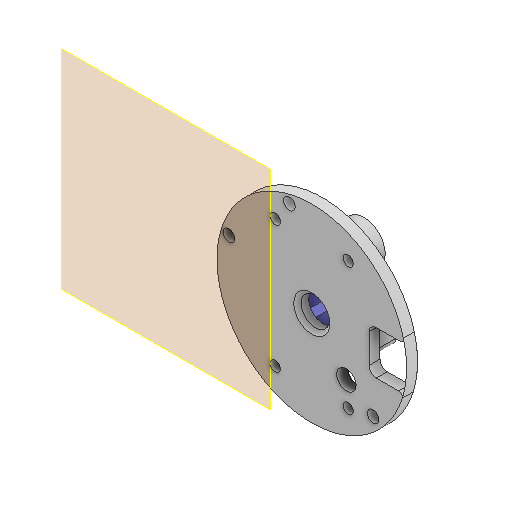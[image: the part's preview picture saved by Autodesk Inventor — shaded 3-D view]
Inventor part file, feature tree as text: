
AUTODESK INVENTOR PART (.ipt)
format: ipt  version: 2022 (Build 260153000, 153)  size: 510,976 bytes
history: native  units: in
note: dims shown in document units (in); Inventor stores cm internally (conversion verified against a paired STEP export)
features: reference x12, extrude x8, sketch x7, other x5, plane x4, fillet x1, chamfer x1, projected_geometry x1
ambient origin geometry x8: Origin, YZ Plane, XZ Plane, XY Plane, X Axis, Y Axis, Z Axis, Center Point
bodies: Solid1 (feature_tree)
feature tree (39):
  plane  "Work Plane1"
  extrude  "Extrusion1"  Depth=0.1181in
  extrude  "Extrusion2"  Depth=1.0in
  plane  "Arbeitsebene4"
  extrude  "Extrusion5"  TaperAngle=0.0deg  [1 undecoded]
  plane  "Arbeitsebene3"
  extrude  "Extrusion6"  Depth=0.126in
  plane  "Arbeitsebene2"
  extrude  "Extrusion7"  Depth=0.0787in
  extrude  "Extrusion10"  Depth=0.0394in TaperAngle=0.0deg
  extrude  "Extrusion11"  Depth=0.3937in
  fillet  "Rundung1"  Radius=0.3543in
  chamfer  "Fase4"  Distance=0.7165in
  extrude  "Extrusion14"  Depth=0.1181in
  sketch  "Sketch1"  dims[d0=0.1181in d1=0.0in d2=0.315in]
  reference  "Reference1"
  reference  "Reference2"
  reference  "Reference3"
  reference  "Reference4"
  reference  "Reference5"
  reference  "Reference6"
  reference  "Reference7"
  reference  "Reference8"
  sketch  "Sketch2"  dims[d3=0.311in d4=1.0in d5=-0.0137in]
  sketch  "Sketch7"  dims[d30=0.1102in d31=0.0in d32=0.0in]
  sketch  "Sketch8"  dims[d33=0.126in d34=0.126in]
  sketch  "Sketch9"  dims[d35=0.0in d36=0.0in d37=0.0787in]
  sketch  "Skizze12"  dims[d38=0.0004in d39=0.0in d51=0.0394in d52=0.0in]
  projected_geometry  "Projizierte Kontur2"
  sketch  "Skizze16"  dims[d53=0.2638in d54=0.3937in d55=0.3543in d56=0.0in d65=0.7165in d66=0.7165in d67=0.0787in d68=0.0787in d71=0.315in d72=0.315in d73=0.315in d74=0.315in d75=0.0394in d76=0.0787in d77=45.0deg d78=0.126in d79=0.1181in d80=0.0in d81=0.0197in d82=0.0344in]
  reference  "Referenz30"
  reference  "Referenz31"
  reference  "Referenz32"
  reference  "Referenz33"
  other  "Assembly1"
  other  "Assembly_MANATEE_V0_Manatee_middle2_v0_18:1"
  other  "Anglerfish_lunchbox_m12large_flipped_v0.iam"
  other  "Anglerfish_flipped_LidMoun:1"
  other  "Matchboxscope_M12_Lensadapter_v0:1"
note: 1 required parameter value undecoded (feature->parameter linkage not recoverable at this tier; creation-order binding heuristic only, values carry confidence <= 0.55)
